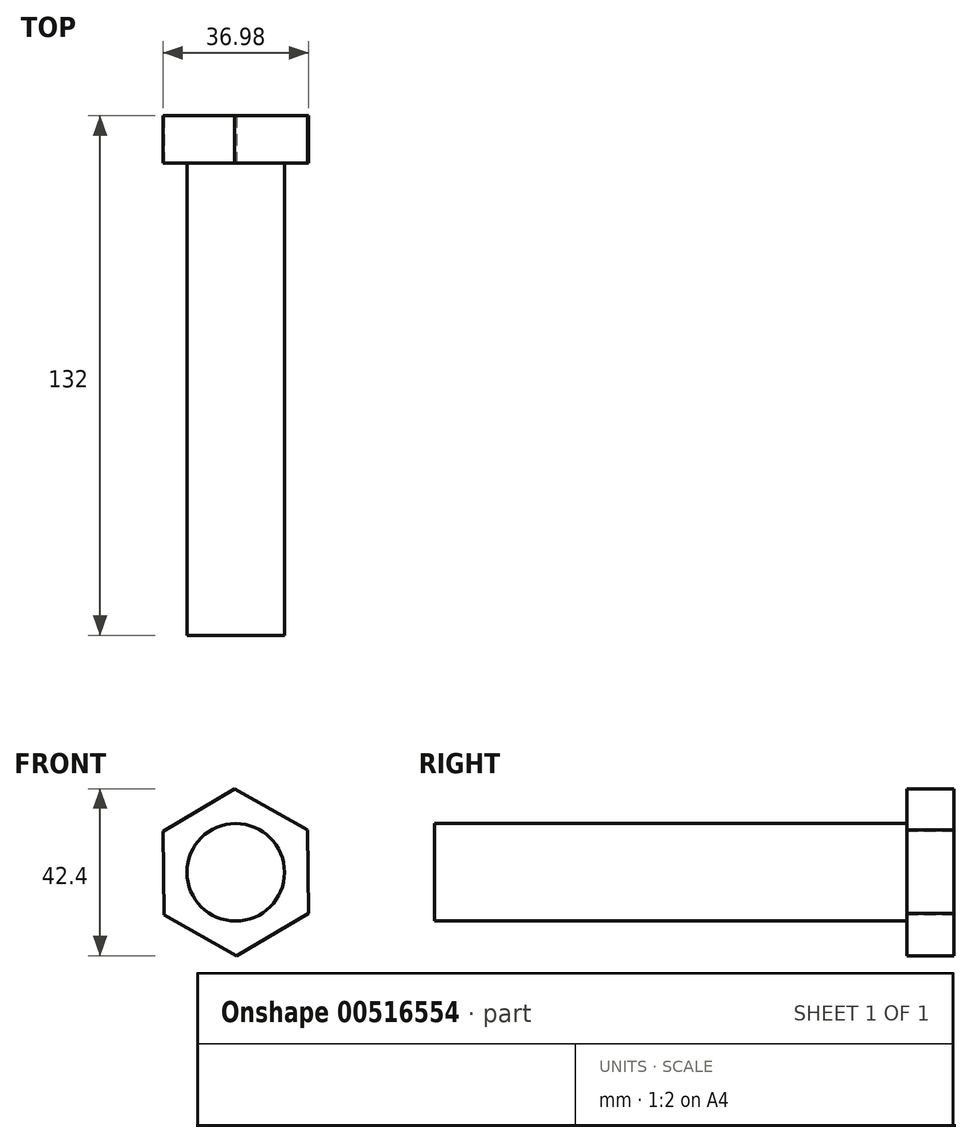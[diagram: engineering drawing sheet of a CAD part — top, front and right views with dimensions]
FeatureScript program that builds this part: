
annotation { "Feature Type Name" : "Feature", "Feature Type Description" : "" }
export const myFeature = defineFeature(function(context is Context, id is Id, definition is map)
    precondition{}
    {
        {
            var Q0;
            Q0=qCreatedBy(makeId("Front.planeOp"),FACE);
            var sketch = newSketch(context, id + "F0", { "sketchPlane" : qUnion([Q0])});
            skCircle(sketch, "E0.cCircle", {"center": v(0, 0) * mm, "radius": 18.36 * mm, "construction": true});
            skLineSegment(sketch, "E0.0", {"start": v(-18.49, 10.38) * mm, "end": v(-0.25, 21.2) * mm});
            skLineSegment(sketch, "E0.1", {"start": v(-0.25, 21.2) * mm, "end": v(18.24, 10.82) * mm});
            skLineSegment(sketch, "E0.2", {"start": v(18.24, 10.82) * mm, "end": v(18.49, -10.38) * mm});
            skLineSegment(sketch, "E0.3", {"start": v(18.49, -10.38) * mm, "end": v(0.25, -21.2) * mm});
            skLineSegment(sketch, "E0.4", {"start": v(0.25, -21.2) * mm, "end": v(-18.24, -10.82) * mm});
            skLineSegment(sketch, "E0.5", {"start": v(-18.24, -10.82) * mm, "end": v(-18.49, 10.38) * mm});
            skPoint(sketch, "E0.0.midPoint", {"position": v(-9.37, 15.8) * mm});
            skSolve(sketch);
        }
        {
            var Q0;
            Q0=makeQuery(id+"F0.imprint","IMPRINT",FACE,{"disambiguationData":[TD([[makeQuery(id+"F0.imprint","IMPRINT",EDGE,{"derivedFrom":sQuery(id+"F0.wireOp",EDGE,"E0.0")}),-1.0]])]});
            extrude(context, id + "F1", {"entities" : qUnion([Q0]), "oppositeDirection" : true, "depth" : 12 * mm, "offsetDistance" : 25 * mm});
        }
        {
            var Q0;
            Q0=makeQuery(id+"F0.imprint","IMPRINT",FACE,{"disambiguationData":[TD([[makeQuery(id+"F0.imprint","IMPRINT",EDGE,{"derivedFrom":sQuery(id+"F0.wireOp",EDGE,"E0.0")}),-1.0]])]});
            var sketch = newSketch(context, id + "F2", { "sketchPlane" : qUnion([Q0])});
            skCircle(sketch, "E1", {"center": v(0, 0) * mm, "radius": 12.4 * mm});
            skSolve(sketch);
        }
        {
            var Q0;
            Q0 = qSketchRegion(id + "F2", true);
            extrude(context, id + "F3", {"entities" : qUnion([Q0]), "operationType" : NewBodyOperationType.ADD, "depth" : 120 * mm, "offsetDistance" : 25 * mm});
        }
    });
